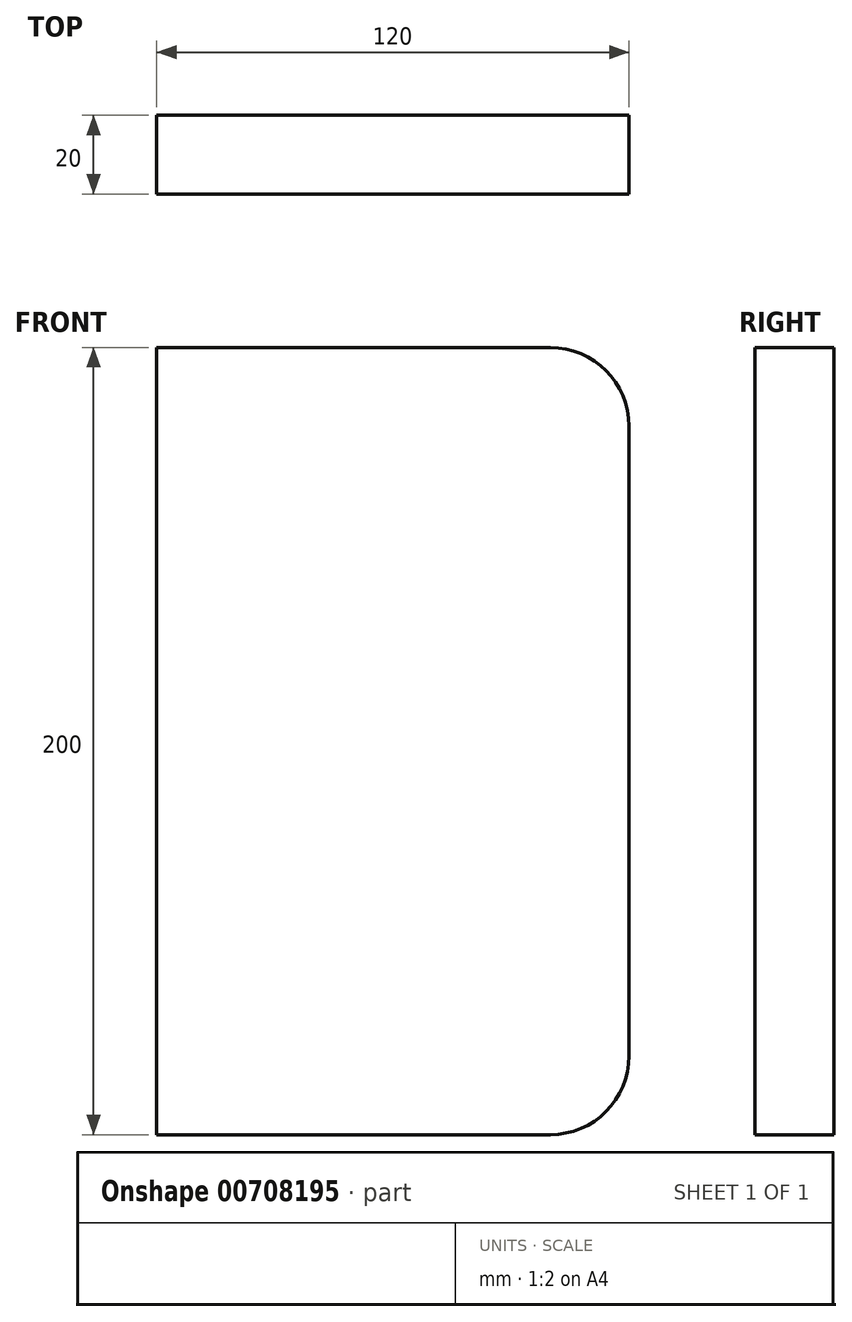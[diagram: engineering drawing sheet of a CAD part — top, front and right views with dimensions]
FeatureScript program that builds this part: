
annotation { "Feature Type Name" : "Feature", "Feature Type Description" : "" }
export const myFeature = defineFeature(function(context is Context, id is Id, definition is map)
    precondition{}
    {
        {
            var Q0;
            Q0=qCreatedBy(makeId("Front.planeOp"),FACE);
            var sketch = newSketch(context, id + "F0", { "sketchPlane" : qUnion([Q0])});
            skLineSegment(sketch, "E0.bottom", {"start": v(-60, 100) * mm, "end": v(60, 100) * mm});
            skLineSegment(sketch, "E0.top", {"start": v(-60, -100) * mm, "end": v(60, -100) * mm});
            skLineSegment(sketch, "E0.left", {"start": v(-60, 100) * mm, "end": v(-60, -100) * mm});
            skLineSegment(sketch, "E0.right", {"start": v(60, 100) * mm, "end": v(60, -100) * mm});
            skSolve(sketch);
        }
        {
            var Q0;
            Q0=makeQuery(id+"F0.imprint","IMPRINT",FACE,{"disambiguationData":[TD([[makeQuery(id+"F0.imprint","IMPRINT",EDGE,{"derivedFrom":sQuery(id+"F0.wireOp",EDGE,"E0.bottom")}),-1.0]])]});
            extrude(context, id + "F1", {"entities" : qUnion([Q0]), "endBound" : BoundingType.SYMMETRIC, "depth" : 20 * mm, "offsetDistance" : 25 * mm});
        }
        {
            var Q0;
            Q0=makeQuery(id+"F1.opExtrude","SWEPT_EDGE",EDGE,{"disambiguationData":[OSD([sQuery(id+"F0.wireOp",EDGE,"E0.bottom"),sQuery(id+"F0.wireOp",EDGE,"E0.right")])]});
            var Q1;
            Q1=makeQuery(id+"F1.opExtrude","SWEPT_EDGE",EDGE,{"disambiguationData":[OSD([sQuery(id+"F0.wireOp",EDGE,"E0.top"),sQuery(id+"F0.wireOp",EDGE,"E0.right")])]});
            fillet(context, id + "F2", {"entities" : qUnion([Q0, Q1]), "radius" : 20 * mm, "tangentPropagation" : true, "allowEdgeOverflow" : false});
        }
    });
